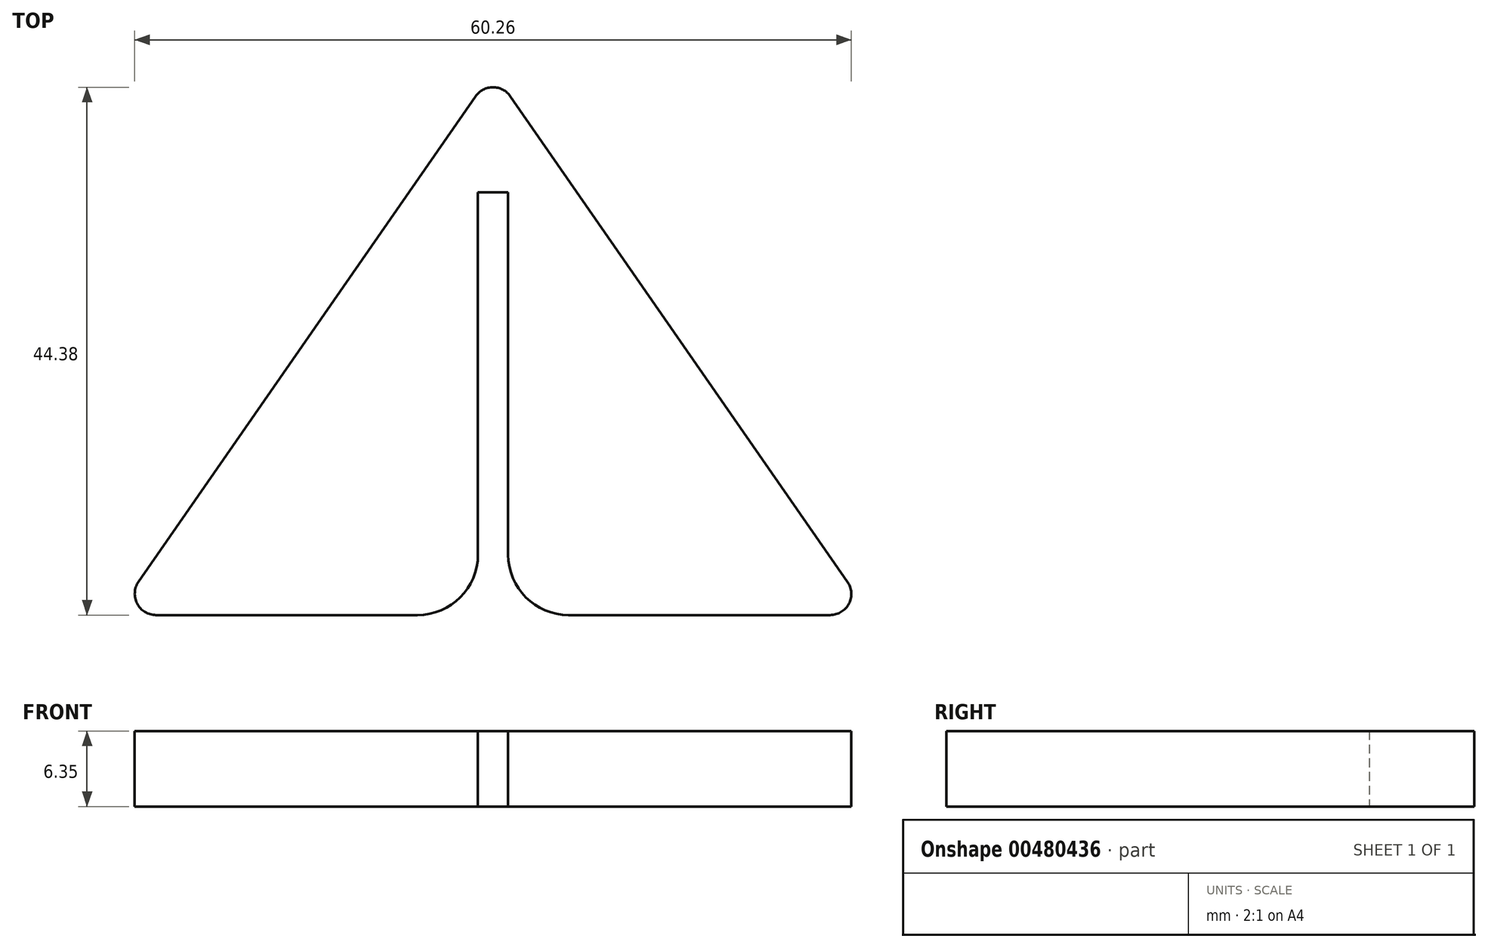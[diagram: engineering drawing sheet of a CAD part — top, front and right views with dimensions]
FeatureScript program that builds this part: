
annotation { "Feature Type Name" : "Feature", "Feature Type Description" : "" }
export const myFeature = defineFeature(function(context is Context, id is Id, definition is map)
    precondition{}
    {
        {
            var Q0;
            Q0=qCreatedBy(makeId("Top.planeOp"),FACE);
            var sketch = newSketch(context, id + "F0", { "sketchPlane" : qUnion([Q0])});
            skPoint(sketch, "E0", {"position": v(-1.27, 0) * mm});
            skPoint(sketch, "E1", {"position": v(1.27, 0) * mm});
            skPoint(sketch, "E2", {"position": v(-31.75, 0) * mm});
            skPoint(sketch, "E3", {"position": v(31.75, 0) * mm});
            skPoint(sketch, "E4", {"position": v(0, 45.72) * mm});
            skLineSegment(sketch, "E5", {"start": v(0, 45.72) * mm, "end": v(-31.75, 0) * mm});
            skLineSegment(sketch, "E6", {"start": v(-31.75, 0) * mm, "end": v(-1.27, 0) * mm});
            skLineSegment(sketch, "E7", {"start": v(1.27, 0) * mm, "end": v(31.75, 0) * mm});
            skLineSegment(sketch, "E8", {"start": v(0, 45.72) * mm, "end": v(31.75, 0) * mm});
            skPoint(sketch, "E9", {"position": v(-1.27, 35.56) * mm});
            skPoint(sketch, "E10", {"position": v(1.27, 35.56) * mm});
            skLineSegment(sketch, "E11", {"start": v(-1.27, 35.56) * mm, "end": v(1.27, 35.56) * mm});
            skLineSegment(sketch, "E12", {"start": v(1.27, 0) * mm, "end": v(1.27, 35.56) * mm});
            skLineSegment(sketch, "E13", {"start": v(-1.27, 35.56) * mm, "end": v(-1.27, 0) * mm});
            skPoint(sketch, "E14", {"position": v(0, 35.56) * mm});
            skSolve(sketch);
        }
        {
            var Q0;
            Q0=makeQuery(id+"F0.imprint","IMPRINT",FACE,{"disambiguationData":[TD([[makeQuery(id+"F0.imprint","IMPRINT",EDGE,{"derivedFrom":sQuery(id+"F0.wireOp",EDGE,"E5")}),1.0]])]});
            extrude(context, id + "F1", {"entities" : qUnion([Q0]), "depth" : 6.35 * mm});
        }
        {
            var Q0;
            Q0=makeQuery(id+"F1.opExtrude","SWEPT_EDGE",EDGE,{"disambiguationData":[OSD([sQuery(id+"F0.wireOp",EDGE,"E6"),sQuery(id+"F0.wireOp",EDGE,"E13")])]});
            var Q1;
            Q1=makeQuery(id+"F1.opExtrude","SWEPT_EDGE",EDGE,{"disambiguationData":[OSD([sQuery(id+"F0.wireOp",EDGE,"E7"),sQuery(id+"F0.wireOp",EDGE,"E12")])]});
            fillet(context, id + "F2", {"entities" : qUnion([Q0, Q1]), "radius" : 5.08 * mm, "tangentPropagation" : true, "allowEdgeOverflow" : false});
        }
        {
            var Q0;
            Q0=makeQuery(id+"F1.opExtrude","SWEPT_EDGE",EDGE,{"disambiguationData":[OSD([sQuery(id+"F0.wireOp",EDGE,"E5"),sQuery(id+"F0.wireOp",EDGE,"E8")])]});
            var Q1;
            Q1=makeQuery(id+"F1.opExtrude","SWEPT_EDGE",EDGE,{"disambiguationData":[OSD([sQuery(id+"F0.wireOp",EDGE,"E7"),sQuery(id+"F0.wireOp",EDGE,"E8")])]});
            var Q2;
            Q2=makeQuery(id+"F1.opExtrude","SWEPT_EDGE",EDGE,{"disambiguationData":[OSD([sQuery(id+"F0.wireOp",EDGE,"E5"),sQuery(id+"F0.wireOp",EDGE,"E6")])]});
            fillet(context, id + "F3", {"entities" : qUnion([Q0, Q1, Q2]), "radius" : 1.78 * mm, "tangentPropagation" : true, "allowEdgeOverflow" : false});
        }
    });
